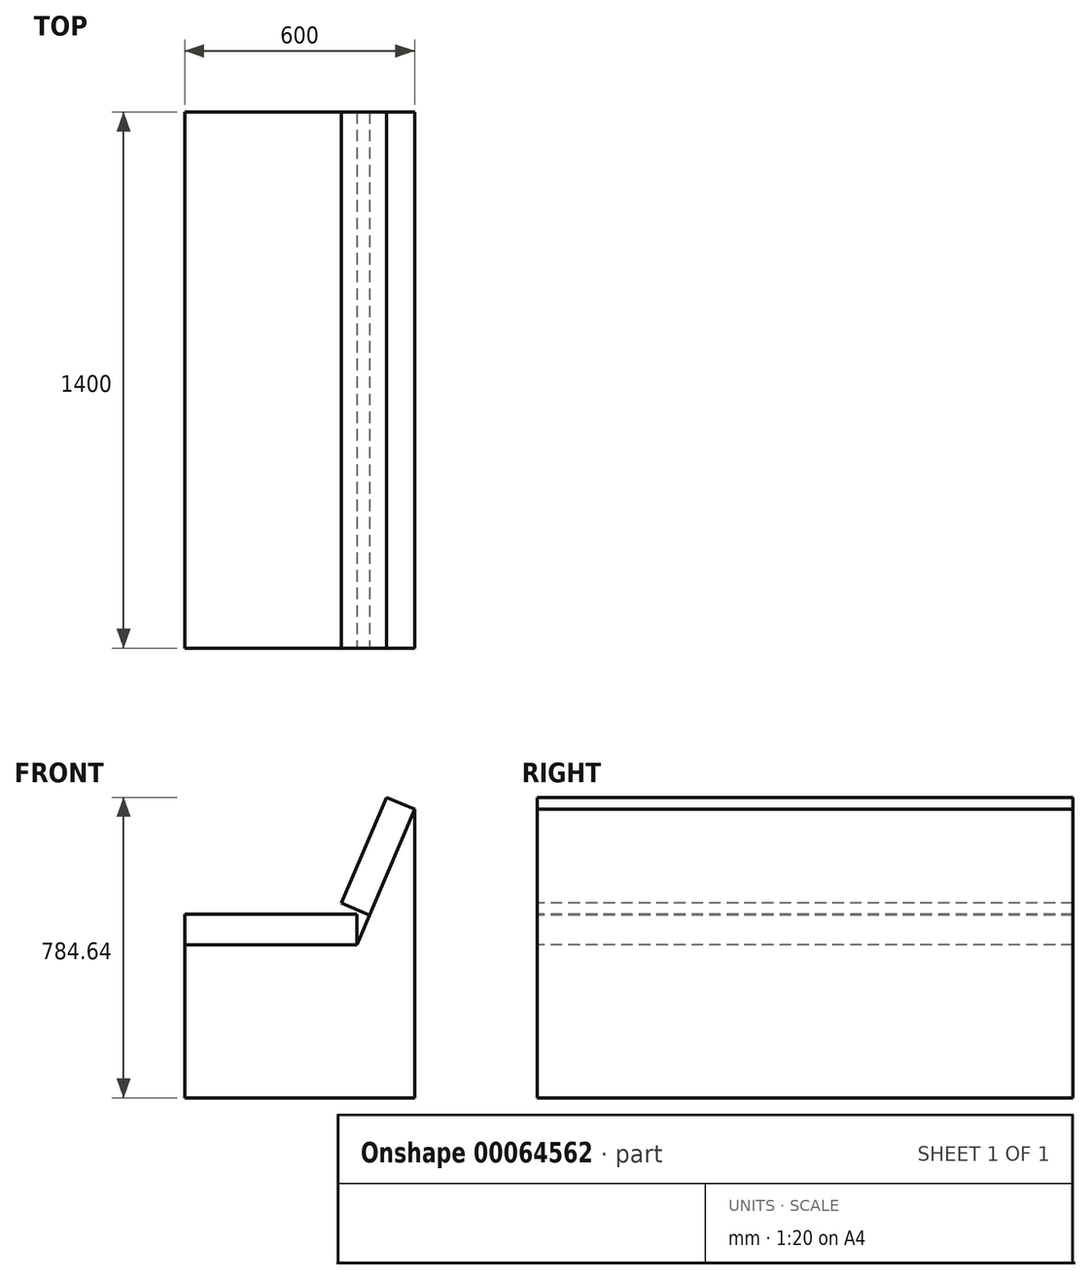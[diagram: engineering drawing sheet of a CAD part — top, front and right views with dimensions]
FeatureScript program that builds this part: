
annotation { "Feature Type Name" : "Feature", "Feature Type Description" : "" }
export const myFeature = defineFeature(function(context is Context, id is Id, definition is map)
    precondition{}
    {
        {
            var Q0;
            Q0=qCreatedBy(makeId("Front.planeOp"),FACE);
            var sketch = newSketch(context, id + "F0", { "sketchPlane" : qUnion([Q0])});
            skLineSegment(sketch, "E0.bottom", {"start": v(0, 0) * mm, "end": v(600, 0) * mm});
            skLineSegment(sketch, "E0.top", {"start": v(0, 400) * mm, "end": v(600, 400) * mm});
            skLineSegment(sketch, "E0.left", {"start": v(0, 0) * mm, "end": v(0, 400) * mm});
            skLineSegment(sketch, "E0.right", {"start": v(600, 0) * mm, "end": v(600, 400) * mm});
            skLineSegment(sketch, "E1", {"start": v(450, 400) * mm, "end": v(600, 753.38) * mm});
            skLineSegment(sketch, "E2", {"start": v(600, 753.38) * mm, "end": v(600, 400) * mm});
            skLineSegment(sketch, "E3", {"start": v(0, 400) * mm, "end": v(0, 480) * mm});
            skLineSegment(sketch, "E4", {"start": v(0, 480) * mm, "end": v(450, 480) * mm});
            skLineSegment(sketch, "E5", {"start": v(450, 480) * mm, "end": v(450, 400) * mm});
            skLineSegment(sketch, "E6", {"start": v(600, 753.38) * mm, "end": v(526.36, 784.64) * mm});
            skLineSegment(sketch, "E7", {"start": v(526.36, 784.64) * mm, "end": v(409.14, 508.48) * mm});
            skLineSegment(sketch, "E8", {"start": v(409.14, 508.48) * mm, "end": v(482.78, 477.23) * mm});
            skSolve(sketch);
        }
        {
            var Q0;
            Q0=makeQuery(id+"F0.imprint","IMPRINT",FACE,{"disambiguationData":[TD([[makeQuery(id+"F0.imprint","IMPRINT",EDGE,{"derivedFrom":sQuery(id+"F0.wireOp",EDGE,"E0.bottom")}),1.0]])]});
            var Q1;
            {var subQ0=sQuery(id+"F0.wireOp",EDGE,"E2");Q1=makeQuery(id+"F0.imprint","IMPRINT",FACE,{"disambiguationData":[TD([[makeQuery(id+"F0.imprint","IMPRINT",EDGE,{"derivedFrom":subQ0}),-1.0]])]});}
            extrude(context, id + "F1", {"entities" : qUnion([Q0, Q1]), "depth" : 1400 * mm});
        }
        {
            var Q0;
            Q0=makeQuery(id+"F1.opExtrude","CAP_FACE",FACE,{"disambiguationData":[OSD([sQuery(id+"F0.wireOp",EDGE,"E0.bottom"),sQuery(id+"F0.wireOp",EDGE,"E0.top"),sQuery(id+"F0.wireOp",EDGE,"E0.left"),sQuery(id+"F0.wireOp",EDGE,"E0.right"),sQuery(id+"F0.wireOp",EDGE,"E1"),sQuery(id+"F0.wireOp",EDGE,"E2")])],"isStart":false});
            var sketch = newSketch(context, id + "F2", { "sketchPlane" : qUnion([Q0])});
            skLineSegment(sketch, "E9.bottom", {"start": v(0, 400) * mm, "end": v(450, 400) * mm});
            skLineSegment(sketch, "E9.top", {"start": v(0, 480) * mm, "end": v(450, 480) * mm});
            skLineSegment(sketch, "E9.left", {"start": v(0, 400) * mm, "end": v(0, 480) * mm});
            skLineSegment(sketch, "E9.right", {"start": v(450, 400) * mm, "end": v(450, 480) * mm});
            skLineSegment(sketch, "E10", {"start": v(600, 753.38) * mm, "end": v(482.78, 477.23) * mm});
            skLineSegment(sketch, "E11", {"start": v(482.78, 477.23) * mm, "end": v(409.14, 508.48) * mm});
            skLineSegment(sketch, "E12", {"start": v(409.14, 508.48) * mm, "end": v(526.36, 784.64) * mm});
            skLineSegment(sketch, "E13", {"start": v(526.36, 784.64) * mm, "end": v(600, 753.38) * mm});
            skSolve(sketch);
        }
        {
            var Q0;
            Q0=makeQuery(id+"F2.imprint","IMPRINT",FACE,{"disambiguationData":[TD([[makeQuery(id+"F2.imprint","IMPRINT",EDGE,{"derivedFrom":sQuery(id+"F2.wireOp",EDGE,"E9.bottom")}),1.0]])]});
            var Q1;
            Q1=makeQuery(id+"F2.imprint","IMPRINT",FACE,{"disambiguationData":[TD([[makeQuery(id+"F2.imprint","IMPRINT",EDGE,{"derivedFrom":sQuery(id+"F2.wireOp",EDGE,"E10")}),1.0]])]});
            extrude(context, id + "F3", {"entities" : qUnion([Q0, Q1]), "oppositeDirection" : true, "depth" : 1400 * mm});
        }
    });
